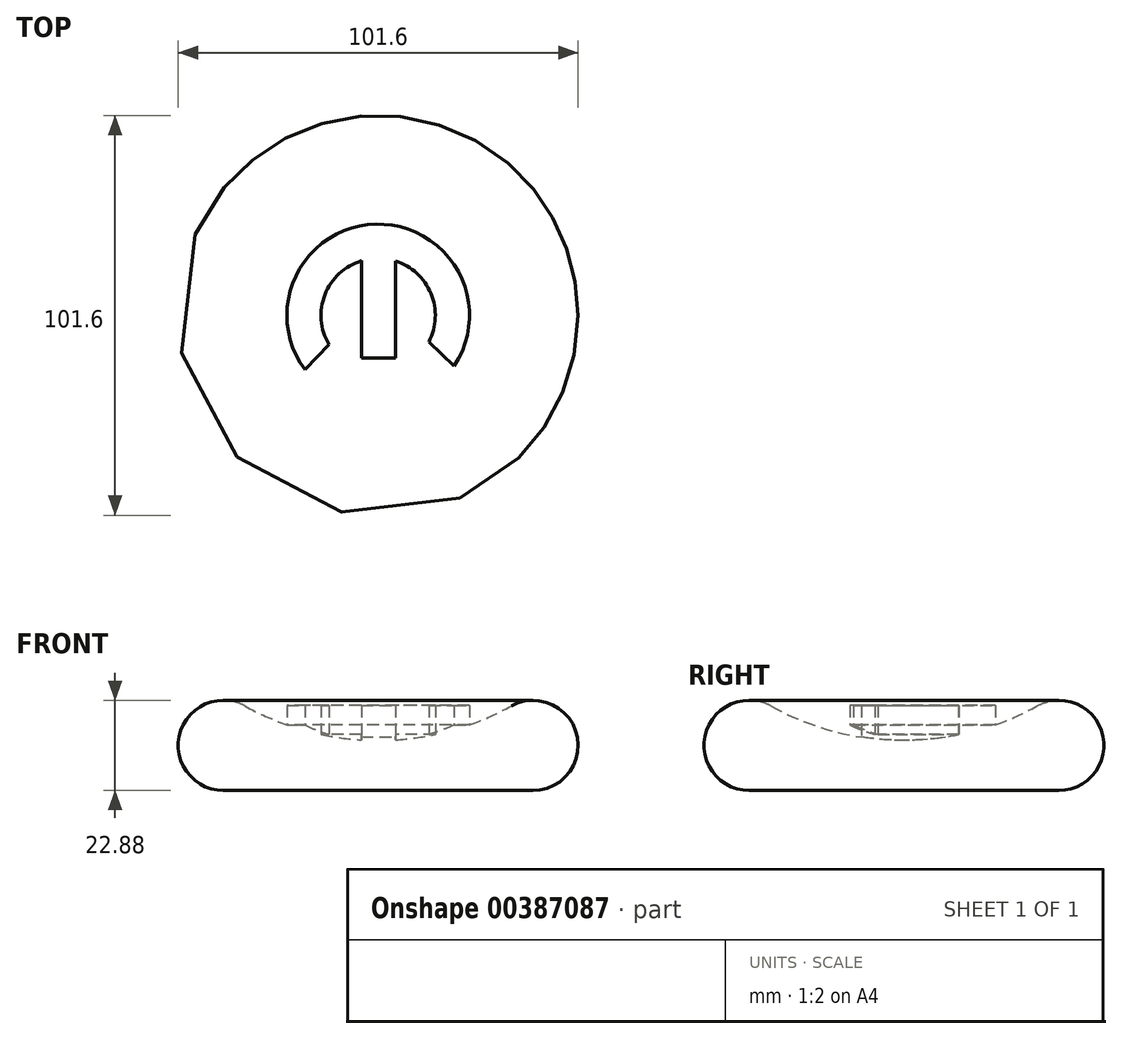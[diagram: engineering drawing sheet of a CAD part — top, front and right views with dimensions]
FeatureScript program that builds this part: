
annotation { "Feature Type Name" : "Feature", "Feature Type Description" : "" }
export const myFeature = defineFeature(function(context is Context, id is Id, definition is map)
    precondition{}
    {
        {
            var Q0;
            Q0=qCreatedBy(makeId("Front.planeOp"),FACE);
            var sketch = newSketch(context, id + "F0", { "sketchPlane" : qUnion([Q0])});
            skArc(sketch, "E0", {"start": v(-33.81, 21.45) * mm, "mid": v(-50.44, 14.3) * mm, "end": v(-39.36, 0) * mm});
            skArc(sketch, "E1", {"start": v(-33.81, 21.45) * mm, "mid": v(-17.46, 14.92) * mm, "end": v(0, 12.7) * mm});
            skLineSegment(sketch, "E2", {"start": v(0, 0) * mm, "end": v(-39.36, 0) * mm});
            skLineSegment(sketch, "E3", {"start": v(-39.36, 0) * mm, "end": v(0, 0) * mm});
            skLineSegment(sketch, "E4", {"start": v(0, 12.7) * mm, "end": v(0, 0) * mm});
            skSolve(sketch);
        }
        {
            var Q0;
            Q0=makeQuery(id+"F0.imprint","IMPRINT",FACE,{"disambiguationData":[TD([[makeQuery(id+"F0.imprint","IMPRINT",EDGE,{"derivedFrom":sQuery(id+"F0.wireOp",EDGE,"E0")}),1.0]])]});
            var Q1;
            Q1=sQuery(id+"F0.wireOp",EDGE,"E4");
            revolve(context, id + "F1", {"entities" : qUnion([Q0]), "axis" : qUnion([Q1]), "revolveType" : RevolveType.FULL});
        }
        {
            var Q0;
            Q0=qCreatedBy(makeId("Top.planeOp"),FACE);
            cPlane(context, id + "F2", {"entities" : qUnion([Q0]), "cplaneType" : CPlaneType.OFFSET, "offset" : 8.9 * mm, "width" : 152.4 * mm, "height" : 152.4 * mm});
        }
        {
            var Q0;
            Q0=qCreatedBy(id+"F2.planeOp",FACE);
            var sketch = newSketch(context, id + "F3", { "sketchPlane" : qUnion([Q0])});
            skArc(sketch, "E5", {"start": v(19.33, -12.82) * mm, "mid": v(-0.6, 23.18) * mm, "end": v(-18.64, -13.8) * mm});
            skArc(sketch, "E6", {"start": v(12.88, -6.7) * mm, "mid": v(13.41, 5.55) * mm, "end": v(4.38, 13.84) * mm});
            skLineSegment(sketch, "E7", {"start": v(-12.52, -7.35) * mm, "end": v(-18.64, -13.8) * mm});
            skLineSegment(sketch, "E8", {"start": v(12.88, -6.7) * mm, "end": v(19.33, -12.82) * mm});
            skLineSegment(sketch, "E9", {"start": v(-4.25, 13.88) * mm, "end": v(-4.25, -10.77) * mm});
            skLineSegment(sketch, "E10", {"start": v(-4.25, -10.77) * mm, "end": v(4.38, -10.77) * mm});
            skLineSegment(sketch, "E11", {"start": v(4.38, -10.77) * mm, "end": v(4.38, 13.84) * mm});
            skArc(sketch, "E12.trimOffspring", {"start": v(-4.25, 13.88) * mm, "mid": v(-13.53, 5.27) * mm, "end": v(-12.52, -7.35) * mm});
            skSolve(sketch);
        }
        {
            var Q0;
            Q0 = qSketchRegion(id + "F3", true);
            extrude(context, id + "F4", {"entities" : qUnion([Q0]), "depth" : 12.7 * mm});
        }
        {
            var Q0;
            Q0 = qSketchRegion(id + "F3", true);
            extrude(context, id + "F5", {"entities" : qUnion([Q0]), "operationType" : NewBodyOperationType.ADD, "depth" : 0.76 * mm});
        }
    });
